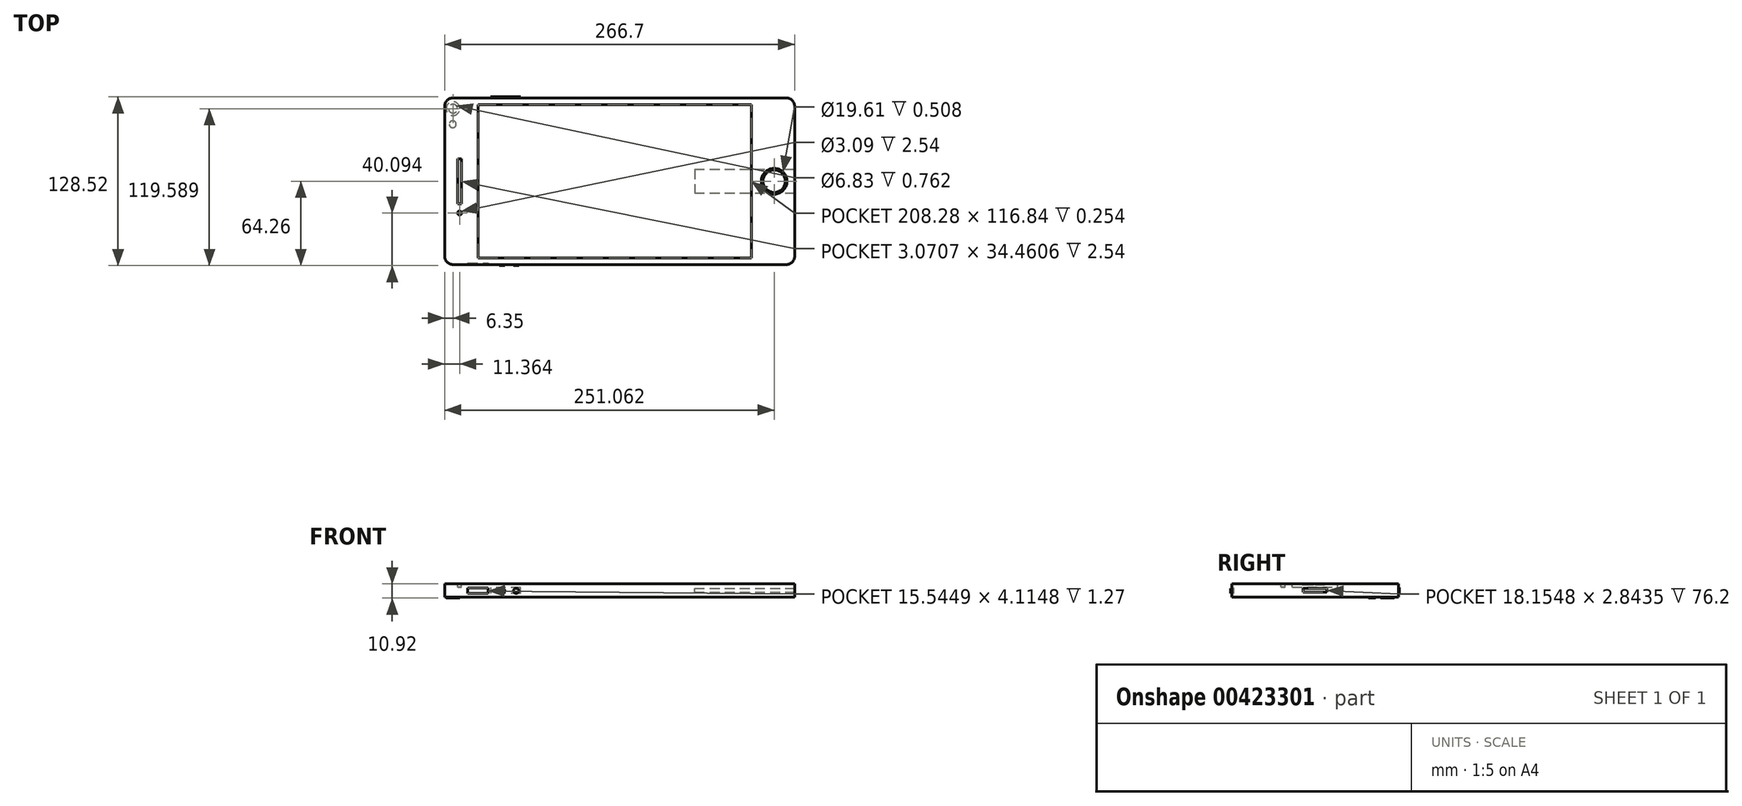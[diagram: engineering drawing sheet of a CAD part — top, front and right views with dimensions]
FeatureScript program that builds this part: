
annotation { "Feature Type Name" : "Feature", "Feature Type Description" : "" }
export const myFeature = defineFeature(function(context is Context, id is Id, definition is map)
    precondition{}
    {
        {
            var Q0;
            Q0=qCreatedBy(makeId("Top.planeOp"),FACE);
            var sketch = newSketch(context, id + "F0", { "sketchPlane" : qUnion([Q0])});
            skLineSegment(sketch, "E0", {"start": v(-133.35, -50.8) * mm, "end": v(-133.35, 50.8) * mm});
            skLineSegment(sketch, "E1", {"start": v(-120.65, -63.5) * mm, "end": v(120.65, -63.5) * mm});
            skLineSegment(sketch, "E2", {"start": v(-133.35, -50.8) * mm, "end": v(-133.35, -57.15) * mm});
            skLineSegment(sketch, "E3", {"start": v(-120.65, -63.5) * mm, "end": v(-127, -63.5) * mm});
            skArc(sketch, "E4.filletArc", {"start": v(-133.35, -57.15) * mm, "mid": v(-131.5, -61.64) * mm, "end": v(-127, -63.5) * mm});
            skPoint(sketch, "E5", {"position": v(0, -63.5) * mm});
            skPoint(sketch, "E6", {"position": v(-133.35, 0) * mm});
            skLineSegment(sketch, "E7", {"start": v(-133.35, 0) * mm, "end": v(110.5, 0) * mm});
            skLineSegment(sketch, "E8", {"start": v(0, -63.5) * mm, "end": v(0, 109.27) * mm});
            skPoint(sketch, "E9", {"position": v(0, 0) * mm});
            skLineSegment(sketch, "E10.MirrorCS", {"start": v(-120.65, 63.5) * mm, "end": v(120.65, 63.5) * mm});
            skArc(sketch, "E11.MirrorCS", {"start": v(-133.35, 57.15) * mm, "mid": v(-131.5, 61.64) * mm, "end": v(-127, 63.5) * mm});
            skLineSegment(sketch, "E12.MirrorCS", {"start": v(-120.65, 63.5) * mm, "end": v(-127, 63.5) * mm});
            skLineSegment(sketch, "E13.MirrorCS", {"start": v(-133.35, 50.8) * mm, "end": v(-133.35, 57.15) * mm});
            skLineSegment(sketch, "E14.MirrorCS", {"start": v(-133.35, 50.8) * mm, "end": v(-133.35, -50.8) * mm});
            skLineSegment(sketch, "E15.MirrorCS", {"start": v(133.35, 50.8) * mm, "end": v(133.35, -50.8) * mm});
            skArc(sketch, "E16.MirrorCS", {"start": v(133.35, 57.15) * mm, "mid": v(131.5, 61.64) * mm, "end": v(127, 63.5) * mm});
            skLineSegment(sketch, "E17.MirrorCS", {"start": v(133.35, -50.8) * mm, "end": v(133.35, -57.15) * mm});
            skLineSegment(sketch, "E18.MirrorCS", {"start": v(120.65, -63.5) * mm, "end": v(127, -63.5) * mm});
            skLineSegment(sketch, "E19.MirrorCS", {"start": v(133.35, 50.8) * mm, "end": v(133.35, 57.15) * mm});
            skLineSegment(sketch, "E20.MirrorCS", {"start": v(120.65, 63.5) * mm, "end": v(127, 63.5) * mm});
            skArc(sketch, "E21.MirrorCS", {"start": v(133.35, -57.15) * mm, "mid": v(131.5, -61.64) * mm, "end": v(127, -63.5) * mm});
            skSolve(sketch);
        }
        {
            var Q0;
            Q0 = qSketchRegion(id + "F0", true);
            extrude(context, id + "F1", {"entities" : qUnion([Q0]), "depth" : 10.16 * mm});
        }
        {
            var Q0;
            Q0=makeQuery(id+"F1.opExtrude","CAP_FACE",FACE,{"disambiguationData":[OSD([sQuery(id+"F0.wireOp",EDGE,"E1"),sQuery(id+"F0.wireOp",EDGE,"E2"),sQuery(id+"F0.wireOp",EDGE,"E3"),sQuery(id+"F0.wireOp",EDGE,"E4.filletArc"),sQuery(id+"F0.wireOp",EDGE,"E10.MirrorCS"),sQuery(id+"F0.wireOp",EDGE,"E11.MirrorCS"),sQuery(id+"F0.wireOp",EDGE,"E12.MirrorCS"),sQuery(id+"F0.wireOp",EDGE,"E13.MirrorCS"),sQuery(id+"F0.wireOp",EDGE,"E14.MirrorCS"),sQuery(id+"F0.wireOp",EDGE,"E15.MirrorCS"),sQuery(id+"F0.wireOp",EDGE,"E16.MirrorCS"),sQuery(id+"F0.wireOp",EDGE,"E19.MirrorCS"),sQuery(id+"F0.wireOp",EDGE,"E20.MirrorCS"),sQuery(id+"F0.wireOp",EDGE,"E21.MirrorCS"),sQuery(id+"F0.wireOp",EDGE,"E17.MirrorCS"),sQuery(id+"F0.wireOp",EDGE,"E18.MirrorCS")])],"isStart":false});
            var sketch = newSketch(context, id + "F2", { "sketchPlane" : qUnion([Q0])});
            skLineSegment(sketch, "E22.MirrorCS", {"start": v(-131.6, 0) * mm, "end": v(-131.6, 30.45) * mm});
            skLineSegment(sketch, "E23", {"start": v(-107.95, 58.42) * mm, "end": v(100.33, 58.42) * mm});
            skLineSegment(sketch, "E24", {"start": v(-107.95, -58.42) * mm, "end": v(100.33, -58.42) * mm});
            skLineSegment(sketch, "E25", {"start": v(-107.95, 58.42) * mm, "end": v(-107.95, -58.42) * mm});
            skLineSegment(sketch, "E26", {"start": v(100.33, 58.42) * mm, "end": v(100.33, -58.42) * mm});
            skSolve(sketch);
        }
        {
            var Q0;
            Q0 = qSketchRegion(id + "F2", true);
            extrude(context, id + "F3", {"entities" : qUnion([Q0]), "operationType" : NewBodyOperationType.REMOVE, "oppositeDirection" : true, "depth" : 0.25 * mm});
        }
        {
            var Q0;
            Q0=makeQuery(id+"F1.opExtrude","CAP_FACE",FACE,{"disambiguationData":[OSD([sQuery(id+"F0.wireOp",EDGE,"E1"),sQuery(id+"F0.wireOp",EDGE,"E2"),sQuery(id+"F0.wireOp",EDGE,"E3"),sQuery(id+"F0.wireOp",EDGE,"E4.filletArc"),sQuery(id+"F0.wireOp",EDGE,"E10.MirrorCS"),sQuery(id+"F0.wireOp",EDGE,"E11.MirrorCS"),sQuery(id+"F0.wireOp",EDGE,"E12.MirrorCS"),sQuery(id+"F0.wireOp",EDGE,"E13.MirrorCS"),sQuery(id+"F0.wireOp",EDGE,"E14.MirrorCS"),sQuery(id+"F0.wireOp",EDGE,"E15.MirrorCS"),sQuery(id+"F0.wireOp",EDGE,"E16.MirrorCS"),sQuery(id+"F0.wireOp",EDGE,"E19.MirrorCS"),sQuery(id+"F0.wireOp",EDGE,"E20.MirrorCS"),sQuery(id+"F0.wireOp",EDGE,"E21.MirrorCS"),sQuery(id+"F0.wireOp",EDGE,"E17.MirrorCS"),sQuery(id+"F0.wireOp",EDGE,"E18.MirrorCS")])],"isStart":false});
            var sketch = newSketch(context, id + "F4", { "sketchPlane" : qUnion([Q0])});
            skCircle(sketch, "E27", {"center": v(117.71, 0) * mm, "radius": 9.8 * mm});
            skCircle(sketch, "E28.0", {"center": v(117.71, 0) * mm, "radius": 8.54 * mm});
            skSolve(sketch);
        }
        {
            var Q0;
            Q0=makeQuery(id+"F4.imprint","IMPRINT",FACE,{"disambiguationData":[TD([[makeQuery(id+"F4.imprint","IMPRINT",EDGE,{"derivedFrom":sQuery(id+"F4.wireOp",EDGE,"E27")}),1.0]])]});
            extrude(context, id + "F5", {"entities" : qUnion([Q0]), "operationType" : NewBodyOperationType.REMOVE, "oppositeDirection" : true, "depth" : 0.5 * mm});
        }
        {
            var Q0;
            Q0=makeQuery(id+"F5.boolean.opBoolean","SPLIT",FACE,{"disambiguationData":[TD([makeQuery(id+"F5.opExtrude","SWEPT_FACE",FACE,{"disambiguationData":[OSD([sQuery(id+"F4.wireOp",EDGE,"E28.0")])]})])],"derivedFrom":makeQuery(id+"F1.opExtrude","CAP_FACE",FACE,{"disambiguationData":[OSD([sQuery(id+"F0.wireOp",EDGE,"E1"),sQuery(id+"F0.wireOp",EDGE,"E2"),sQuery(id+"F0.wireOp",EDGE,"E3"),sQuery(id+"F0.wireOp",EDGE,"E4.filletArc"),sQuery(id+"F0.wireOp",EDGE,"E10.MirrorCS"),sQuery(id+"F0.wireOp",EDGE,"E11.MirrorCS"),sQuery(id+"F0.wireOp",EDGE,"E12.MirrorCS"),sQuery(id+"F0.wireOp",EDGE,"E13.MirrorCS"),sQuery(id+"F0.wireOp",EDGE,"E14.MirrorCS"),sQuery(id+"F0.wireOp",EDGE,"E15.MirrorCS"),sQuery(id+"F0.wireOp",EDGE,"E16.MirrorCS"),sQuery(id+"F0.wireOp",EDGE,"E19.MirrorCS"),sQuery(id+"F0.wireOp",EDGE,"E20.MirrorCS"),sQuery(id+"F0.wireOp",EDGE,"E21.MirrorCS"),sQuery(id+"F0.wireOp",EDGE,"E17.MirrorCS"),sQuery(id+"F0.wireOp",EDGE,"E18.MirrorCS")])],"isStart":false})});
            extrude(context, id + "F6", {"entities" : qUnion([Q0]), "operationType" : NewBodyOperationType.REMOVE, "oppositeDirection" : true, "depth" : 0.25 * mm});
        }
        {
            var Q0;
            Q0=makeQuery(id+"F1.opExtrude","SWEPT_FACE",FACE,{"disambiguationData":[OSD([sQuery(id+"F0.wireOp",EDGE,"E1"),sQuery(id+"F0.wireOp",EDGE,"E3"),sQuery(id+"F0.wireOp",EDGE,"E18.MirrorCS")])]});
            var sketch = newSketch(context, id + "F7", { "sketchPlane" : qUnion([Q0])});
            skLineSegment(sketch, "E29.bottom", {"start": v(-115.74, 6.86) * mm, "end": v(-100.2, 6.86) * mm});
            skLineSegment(sketch, "E29.top", {"start": v(-115.74, 2.75) * mm, "end": v(-100.2, 2.75) * mm});
            skLineSegment(sketch, "E29.left", {"start": v(-115.74, 6.86) * mm, "end": v(-115.74, 2.75) * mm});
            skLineSegment(sketch, "E29.right", {"start": v(-100.2, 6.86) * mm, "end": v(-100.2, 2.75) * mm});
            skLineSegment(sketch, "E30", {"start": v(-115.74, 4.8) * mm, "end": v(-100.2, 4.8) * mm});
            skSolve(sketch);
        }
        {
            var Q0;
            Q0 = qSketchRegion(id + "F7", true);
            extrude(context, id + "F8", {"entities" : qUnion([Q0]), "operationType" : NewBodyOperationType.REMOVE, "oppositeDirection" : true, "depth" : 1.27 * mm});
        }
        {
            var Q0;
            {var subQ0=sQuery(id+"F7.wireOp",EDGE,"E29.bottom");Q0=makeQuery(id+"F7.imprint","IMPRINT",FACE,{"disambiguationData":[TD([[makeQuery(id+"F7.imprint","IMPRINT",EDGE,{"derivedFrom":subQ0}),-1.0]])]});}
            extrude(context, id + "F9", {"entities" : qUnion([Q0]), "operationType" : NewBodyOperationType.REMOVE, "oppositeDirection" : true, "depth" : 0.25 * mm});
        }
        {
            var Q0;
            Q0=makeQuery(id+"F1.opExtrude","SWEPT_FACE",FACE,{"disambiguationData":[OSD([sQuery(id+"F0.wireOp",EDGE,"E1"),sQuery(id+"F0.wireOp",EDGE,"E3"),sQuery(id+"F0.wireOp",EDGE,"E18.MirrorCS")])]});
            var sketch = newSketch(context, id + "F10", { "sketchPlane" : qUnion([Q0])});
            skCircle(sketch, "E31", {"center": v(-78.86, 4.8) * mm, "radius": 2.02 * mm});
            skPoint(sketch, "E31.centerSnap0", {"position": v(-100.2, 4.8) * mm});
            skCircle(sketch, "E32", {"center": v(-89.52, 4.8) * mm, "radius": 2.02 * mm});
            skSolve(sketch);
        }
        {
            var Q0;
            Q0 = qSketchRegion(id + "F10", true);
            extrude(context, id + "F11", {"entities" : qUnion([Q0]), "operationType" : NewBodyOperationType.ADD, "depth" : 0.76 * mm});
        }
        {
            var Q0;
            {var subQ0=sQuery(id+"F0.wireOp",EDGE,"E21.MirrorCS");var subQ1=sQuery(id+"F0.wireOp",EDGE,"E16.MirrorCS");var subQ2=sQuery(id+"F0.wireOp",EDGE,"E17.MirrorCS");var subQ3=sQuery(id+"F0.wireOp",EDGE,"E19.MirrorCS");var subQ4=sQuery(id+"F0.wireOp",EDGE,"E15.MirrorCS");var subQ5=sQuery(id+"F0.wireOp",EDGE,"E11.MirrorCS");var subQ6=sQuery(id+"F0.wireOp",EDGE,"E18.MirrorCS");var subQ7=sQuery(id+"F0.wireOp",EDGE,"E3");var subQ8=sQuery(id+"F0.wireOp",EDGE,"E1");var subQ9=sQuery(id+"F0.wireOp",EDGE,"E14.MirrorCS");var subQ10=sQuery(id+"F0.wireOp",EDGE,"E13.MirrorCS");var subQ11=sQuery(id+"F0.wireOp",EDGE,"E2");var subQ12=sQuery(id+"F0.wireOp",EDGE,"E4.filletArc");var subQ13=sQuery(id+"F0.wireOp",EDGE,"E20.MirrorCS");var subQ14=sQuery(id+"F0.wireOp",EDGE,"E12.MirrorCS");var subQ15=sQuery(id+"F0.wireOp",EDGE,"E10.MirrorCS");Q0=makeQuery(id+"F5.boolean.opBoolean","SPLIT",FACE,{"disambiguationData":[TD([makeQuery(id+"F1.opExtrude","SWEPT_FACE",FACE,{"disambiguationData":[OSD([subQ12])]})])],"derivedFrom":makeQuery(id+"F1.opExtrude","CAP_FACE",FACE,{"disambiguationData":[OSD([subQ8,subQ11,subQ7,subQ12,subQ15,subQ5,subQ14,subQ10,subQ9,subQ4,subQ1,subQ3,subQ13,subQ0,subQ2,subQ6])],"isStart":false})});}
            var sketch = newSketch(context, id + "F12", { "sketchPlane" : qUnion([Q0])});
            skLineSegment(sketch, "E33.top", {"start": v(-123.51, 17.23) * mm, "end": v(-120.44, 17.23) * mm});
            skLineSegment(sketch, "E33.left", {"start": v(-123.51, 0) * mm, "end": v(-123.51, 17.23) * mm});
            skLineSegment(sketch, "E33.right", {"start": v(-120.44, 0) * mm, "end": v(-120.44, 17.23) * mm});
            skLineSegment(sketch, "E34.MirrorCS", {"start": v(-123.51, 0) * mm, "end": v(-123.51, -17.23) * mm});
            skLineSegment(sketch, "E35.MirrorCS", {"start": v(-123.51, -17.23) * mm, "end": v(-120.44, -17.23) * mm});
            skLineSegment(sketch, "E36.MirrorCS", {"start": v(-120.44, 0) * mm, "end": v(-120.44, -17.23) * mm});
            skSolve(sketch);
        }
        {
            var Q0;
            Q0=makeQuery(id+"F12.imprint","IMPRINT",FACE,{"disambiguationData":[TD([[makeQuery(id+"F12.imprint","IMPRINT",EDGE,{"derivedFrom":sQuery(id+"F12.wireOp",EDGE,"E33.top")}),-1.0]])]});
            extrude(context, id + "F13", {"entities" : qUnion([Q0]), "operationType" : NewBodyOperationType.REMOVE, "oppositeDirection" : true, "depth" : 2.54 * mm});
        }
        {
            var Q0;
            {var subQ0=sQuery(id+"F0.wireOp",EDGE,"E21.MirrorCS");var subQ1=sQuery(id+"F0.wireOp",EDGE,"E16.MirrorCS");var subQ2=sQuery(id+"F0.wireOp",EDGE,"E17.MirrorCS");var subQ3=sQuery(id+"F0.wireOp",EDGE,"E19.MirrorCS");var subQ4=sQuery(id+"F0.wireOp",EDGE,"E15.MirrorCS");var subQ5=sQuery(id+"F0.wireOp",EDGE,"E11.MirrorCS");var subQ6=sQuery(id+"F0.wireOp",EDGE,"E18.MirrorCS");var subQ7=sQuery(id+"F0.wireOp",EDGE,"E3");var subQ8=sQuery(id+"F0.wireOp",EDGE,"E1");var subQ9=sQuery(id+"F0.wireOp",EDGE,"E14.MirrorCS");var subQ10=sQuery(id+"F0.wireOp",EDGE,"E13.MirrorCS");var subQ11=sQuery(id+"F0.wireOp",EDGE,"E2");var subQ12=sQuery(id+"F0.wireOp",EDGE,"E4.filletArc");var subQ13=sQuery(id+"F0.wireOp",EDGE,"E20.MirrorCS");var subQ14=sQuery(id+"F0.wireOp",EDGE,"E12.MirrorCS");var subQ15=sQuery(id+"F0.wireOp",EDGE,"E10.MirrorCS");Q0=makeQuery(id+"F5.boolean.opBoolean","SPLIT",FACE,{"disambiguationData":[TD([makeQuery(id+"F1.opExtrude","SWEPT_FACE",FACE,{"disambiguationData":[OSD([subQ12])]})])],"derivedFrom":makeQuery(id+"F1.opExtrude","CAP_FACE",FACE,{"disambiguationData":[OSD([subQ8,subQ11,subQ7,subQ12,subQ15,subQ5,subQ14,subQ10,subQ9,subQ4,subQ1,subQ3,subQ13,subQ0,subQ2,subQ6])],"isStart":false})});}
            var sketch = newSketch(context, id + "F14", { "sketchPlane" : qUnion([Q0])});
            skCircle(sketch, "E37", {"center": v(-121.99, -24.17) * mm, "radius": 1.54 * mm});
            skSolve(sketch);
        }
        {
            var Q0;
            Q0 = qSketchRegion(id + "F14", true);
            extrude(context, id + "F15", {"entities" : qUnion([Q0]), "operationType" : NewBodyOperationType.REMOVE, "oppositeDirection" : true, "depth" : 2.54 * mm});
        }
        {
            var Q0;
            Q0=makeQuery(id+"F1.opExtrude","SWEPT_FACE",FACE,{"disambiguationData":[OSD([sQuery(id+"F0.wireOp",EDGE,"E15.MirrorCS"),sQuery(id+"F0.wireOp",EDGE,"E19.MirrorCS"),sQuery(id+"F0.wireOp",EDGE,"E17.MirrorCS")])]});
            var sketch = newSketch(context, id + "F16", { "sketchPlane" : qUnion([Q0])});
            skPoint(sketch, "E38.firstSnap0", {"position": v(0, 10.16) * mm});
            skLineSegment(sketch, "E38.bottom", {"start": v(0, 3.72) * mm, "end": v(-9.08, 3.72) * mm});
            skLineSegment(sketch, "E38.top", {"start": v(0, 6.57) * mm, "end": v(-9.08, 6.57) * mm});
            skLineSegment(sketch, "E38.right", {"start": v(-9.08, 3.72) * mm, "end": v(-9.08, 6.57) * mm});
            skLineSegment(sketch, "E39.MirrorCS", {"start": v(0, 6.57) * mm, "end": v(9.08, 6.57) * mm});
            skLineSegment(sketch, "E40.MirrorCS", {"start": v(9.08, 3.72) * mm, "end": v(9.08, 6.57) * mm});
            skLineSegment(sketch, "E41.MirrorCS", {"start": v(0, 3.72) * mm, "end": v(9.08, 3.72) * mm});
            skSolve(sketch);
        }
        {
            var Q0;
            Q0=makeQuery(id+"F16.imprint","IMPRINT",FACE,{"disambiguationData":[TD([[makeQuery(id+"F16.imprint","IMPRINT",EDGE,{"derivedFrom":sQuery(id+"F16.wireOp",EDGE,"E38.bottom")}),-1.0]])]});
            extrude(context, id + "F17", {"entities" : qUnion([Q0]), "operationType" : NewBodyOperationType.REMOVE, "oppositeDirection" : true, "depth" : 76.2 * mm});
        }
        {
            var Q0;
            Q0=makeQuery(id+"F1.opExtrude","SWEPT_FACE",FACE,{"disambiguationData":[OSD([sQuery(id+"F0.wireOp",EDGE,"E10.MirrorCS"),sQuery(id+"F0.wireOp",EDGE,"E12.MirrorCS"),sQuery(id+"F0.wireOp",EDGE,"E20.MirrorCS")])]});
            var sketch = newSketch(context, id + "F18", { "sketchPlane" : qUnion([Q0])});
            skPoint(sketch, "E42.firstSnap0", {"position": v(127, 5.08) * mm});
            skLineSegment(sketch, "E42.top", {"start": v(75.37, 7.41) * mm, "end": v(98.23, 7.41) * mm});
            skLineSegment(sketch, "E42.left", {"start": v(75.37, 5.08) * mm, "end": v(75.37, 7.41) * mm});
            skLineSegment(sketch, "E42.right", {"start": v(98.23, 5.08) * mm, "end": v(98.23, 7.41) * mm});
            skLineSegment(sketch, "E43.MirrorCS", {"start": v(75.37, 5.08) * mm, "end": v(75.37, 2.75) * mm});
            skLineSegment(sketch, "E44.MirrorCS", {"start": v(75.37, 2.75) * mm, "end": v(91.65, 2.75) * mm});
            skLineSegment(sketch, "E45.MirrorCS", {"start": v(98.23, 5.08) * mm, "end": v(98.23, 2.75) * mm});
            skLineSegment(sketch, "E46", {"start": v(98.23, 2.75) * mm, "end": v(91.65, 2.75) * mm});
            skSolve(sketch);
        }
        {
            var Q0;
            Q0=makeQuery(id+"F18.imprint","IMPRINT",FACE,{"disambiguationData":[TD([[makeQuery(id+"F18.imprint","IMPRINT",EDGE,{"derivedFrom":sQuery(id+"F18.wireOp",EDGE,"E42.top")}),-1.0]])]});
            extrude(context, id + "F19", {"entities" : qUnion([Q0]), "operationType" : NewBodyOperationType.ADD, "depth" : 0.76 * mm});
        }
        {
            var Q0;
            Q0=makeQuery(id+"F1.opExtrude","CAP_FACE",FACE,{"disambiguationData":[OSD([sQuery(id+"F0.wireOp",EDGE,"E1"),sQuery(id+"F0.wireOp",EDGE,"E2"),sQuery(id+"F0.wireOp",EDGE,"E3"),sQuery(id+"F0.wireOp",EDGE,"E4.filletArc"),sQuery(id+"F0.wireOp",EDGE,"E10.MirrorCS"),sQuery(id+"F0.wireOp",EDGE,"E11.MirrorCS"),sQuery(id+"F0.wireOp",EDGE,"E12.MirrorCS"),sQuery(id+"F0.wireOp",EDGE,"E13.MirrorCS"),sQuery(id+"F0.wireOp",EDGE,"E14.MirrorCS"),sQuery(id+"F0.wireOp",EDGE,"E15.MirrorCS"),sQuery(id+"F0.wireOp",EDGE,"E16.MirrorCS"),sQuery(id+"F0.wireOp",EDGE,"E19.MirrorCS"),sQuery(id+"F0.wireOp",EDGE,"E20.MirrorCS"),sQuery(id+"F0.wireOp",EDGE,"E21.MirrorCS"),sQuery(id+"F0.wireOp",EDGE,"E17.MirrorCS"),sQuery(id+"F0.wireOp",EDGE,"E18.MirrorCS")])],"isStart":true});
            var sketch = newSketch(context, id + "F20", { "sketchPlane" : qUnion([Q0])});
            skPoint(sketch, "E47.centerSnap0", {"position": v(-133.35, 0) * mm});
            skCircle(sketch, "E48", {"center": v(-127, -55.33) * mm, "radius": 5.2 * mm});
            skCircle(sketch, "E49.0", {"center": v(-127, -55.33) * mm, "radius": 3.41 * mm});
            skSolve(sketch);
        }
        {
            var Q0;
            Q0 = qSketchRegion(id + "F20", true);
            extrude(context, id + "F21", {"entities" : qUnion([Q0]), "operationType" : NewBodyOperationType.ADD, "depth" : 0.76 * mm});
        }
        {
            var Q0;
            Q0 = qSketchRegion(id + "F20", true);
            extrude(context, id + "F22", {"entities" : qUnion([Q0]), "operationType" : NewBodyOperationType.ADD, "depth" : 0.76 * mm});
        }
        {
            var Q0;
            {var subQ0=sQuery(id+"F0.wireOp",EDGE,"E20.MirrorCS");var subQ1=sQuery(id+"F0.wireOp",EDGE,"E12.MirrorCS");var subQ2=sQuery(id+"F0.wireOp",EDGE,"E10.MirrorCS");var subQ3=sQuery(id+"F0.wireOp",EDGE,"E4.filletArc");var subQ4=sQuery(id+"F0.wireOp",EDGE,"E14.MirrorCS");var subQ5=sQuery(id+"F0.wireOp",EDGE,"E13.MirrorCS");var subQ6=sQuery(id+"F0.wireOp",EDGE,"E2");var subQ7=sQuery(id+"F0.wireOp",EDGE,"E18.MirrorCS");var subQ8=sQuery(id+"F0.wireOp",EDGE,"E3");var subQ9=sQuery(id+"F0.wireOp",EDGE,"E1");var subQ10=sQuery(id+"F0.wireOp",EDGE,"E11.MirrorCS");var subQ11=sQuery(id+"F0.wireOp",EDGE,"E17.MirrorCS");var subQ12=sQuery(id+"F0.wireOp",EDGE,"E19.MirrorCS");var subQ13=sQuery(id+"F0.wireOp",EDGE,"E15.MirrorCS");var subQ14=sQuery(id+"F0.wireOp",EDGE,"E16.MirrorCS");var subQ15=sQuery(id+"F0.wireOp",EDGE,"E21.MirrorCS");Q0=makeQuery(id+"F21.boolean.opBoolean","SPLIT",FACE,{"disambiguationData":[TD([makeQuery(id+"F1.opExtrude","SWEPT_FACE",FACE,{"disambiguationData":[OSD([subQ3])]})])],"derivedFrom":makeQuery(id+"F1.opExtrude","CAP_FACE",FACE,{"disambiguationData":[OSD([subQ9,subQ6,subQ8,subQ3,subQ2,subQ10,subQ1,subQ5,subQ4,subQ13,subQ14,subQ12,subQ0,subQ15,subQ11,subQ7])],"isStart":true})});}
            var sketch = newSketch(context, id + "F23", { "sketchPlane" : qUnion([Q0])});
            skCircle(sketch, "E50", {"center": v(-127.23, -43.45) * mm, "radius": 2.66 * mm});
            skSolve(sketch);
        }
        {
            var Q0;
            Q0=makeQuery(id+"F23.imprint","IMPRINT",FACE,{"disambiguationData":[TD([[makeQuery(id+"F23.imprint","IMPRINT",EDGE,{"derivedFrom":sQuery(id+"F23.wireOp",EDGE,"E50")}),1.0]])]});
            extrude(context, id + "F24", {"entities" : qUnion([Q0]), "operationType" : NewBodyOperationType.ADD, "depth" : 0.5 * mm});
        }
    });
